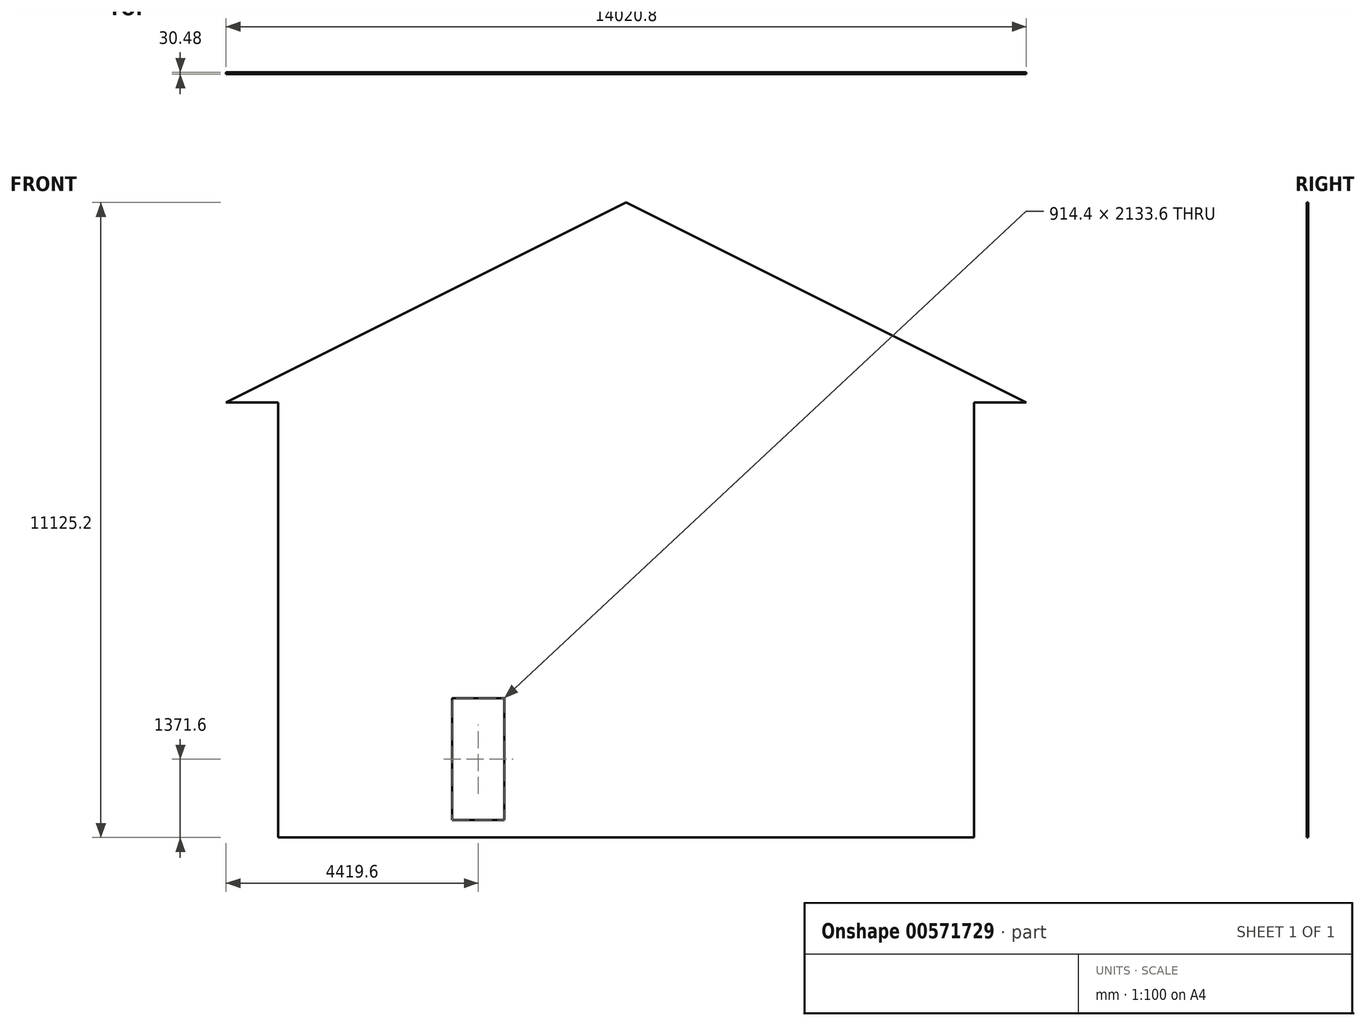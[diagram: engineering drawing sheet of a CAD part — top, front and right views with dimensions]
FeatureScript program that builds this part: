
annotation { "Feature Type Name" : "Feature", "Feature Type Description" : "" }
export const myFeature = defineFeature(function(context is Context, id is Id, definition is map)
    precondition{}
    {
        {
            var Q0;
            Q0=qCreatedBy(makeId("Front.planeOp"),FACE);
            var sketch = newSketch(context, id + "F0", { "sketchPlane" : qUnion([Q0])});
            skLineSegment(sketch, "E0", {"start": v(0, 0) * mm, "end": v(-12192, 0) * mm});
            skLineSegment(sketch, "E1", {"start": v(-12192, 0) * mm, "end": v(-12192, 304.8) * mm});
            skLineSegment(sketch, "E2", {"start": v(0, 0) * mm, "end": v(0, 304.8) * mm});
            skLineSegment(sketch, "E3", {"start": v(0, 304.8) * mm, "end": v(-12192, 304.8) * mm});
            skLineSegment(sketch, "E4", {"start": v(0, 304.8) * mm, "end": v(0, 7620) * mm});
            skLineSegment(sketch, "E5", {"start": v(-12192, 304.8) * mm, "end": v(-12192, 7620) * mm});
            skLineSegment(sketch, "E6", {"start": v(-12192, 7620) * mm, "end": v(0, 7620) * mm});
            skLineSegment(sketch, "E7", {"start": v(-12192, 7620) * mm, "end": v(-13106.4, 7620) * mm});
            skLineSegment(sketch, "E8", {"start": v(0, 7620) * mm, "end": v(914.4, 7620) * mm});
            skLineSegment(sketch, "E9", {"start": v(-6096, 7620) * mm, "end": v(-6096, 10668) * mm});
            skLineSegment(sketch, "E10", {"start": v(-6096, 10668) * mm, "end": v(-6096, 11125.2) * mm});
            skLineSegment(sketch, "E11", {"start": v(-12192, 7620) * mm, "end": v(-6096, 10668) * mm});
            skLineSegment(sketch, "E12", {"start": v(0, 7620) * mm, "end": v(-6096, 10668) * mm});
            skLineSegment(sketch, "E13", {"start": v(914.4, 7620) * mm, "end": v(-6096, 11125.2) * mm});
            skLineSegment(sketch, "E14", {"start": v(-13106.4, 7620) * mm, "end": v(-6096, 11125.2) * mm});
            skLineSegment(sketch, "E15", {"start": v(-9144, 304.8) * mm, "end": v(-9144, 2438.4) * mm});
            skLineSegment(sketch, "E16", {"start": v(-9144, 2438.4) * mm, "end": v(-8229.6, 2438.4) * mm});
            skLineSegment(sketch, "E17", {"start": v(-8229.6, 2438.4) * mm, "end": v(-8229.6, 304.8) * mm});
            skSolve(sketch);
        }
        {
            var Q0;
            Q0=makeQuery(id+"F0.imprint","IMPRINT",FACE,{"disambiguationData":[TD([[makeQuery(id+"F0.imprint","IMPRINT",EDGE,{"derivedFrom":sQuery(id+"F0.wireOp",EDGE,"E0")}),-1.0]])]});
            var Q1;
            Q1=makeQuery(id+"F0.imprint","IMPRINT",FACE,{"disambiguationData":[TD([[makeQuery(id+"F0.imprint","IMPRINT",EDGE,{"derivedFrom":sQuery(id+"F0.wireOp",EDGE,"E7")}),-1.0]])]});
            var Q2;
            Q2=makeQuery(id+"F0.imprint","IMPRINT",FACE,{"disambiguationData":[TD([[makeQuery(id+"F0.imprint","IMPRINT",EDGE,{"derivedFrom":sQuery(id+"F0.wireOp",EDGE,"E8")}),1.0]])]});
            var Q3;
            {var subQ2=sQuery(id+"F0.wireOp",EDGE,"E9");Q3=makeQuery(id+"F0.imprint","IMPRINT",FACE,{"disambiguationData":[TD([[makeQuery(id+"F0.imprint","IMPRINT",EDGE,{"derivedFrom":subQ2}),1.0]])]});}
            var Q4;
            {var subQ2=sQuery(id+"F0.wireOp",EDGE,"E9");Q4=makeQuery(id+"F0.imprint","IMPRINT",FACE,{"disambiguationData":[TD([[makeQuery(id+"F0.imprint","IMPRINT",EDGE,{"derivedFrom":subQ2}),-1.0]])]});}
            var Q5;
            {var subQ2=sQuery(id+"F0.wireOp",EDGE,"E4");Q5=makeQuery(id+"F0.imprint","IMPRINT",FACE,{"disambiguationData":[TD([[makeQuery(id+"F0.imprint","IMPRINT",EDGE,{"derivedFrom":subQ2}),1.0]])]});}
            extrude(context, id + "F1", {"entities" : qUnion([Q0, Q1, Q2, Q3, Q4, Q5]), "depth" : 30.48 * mm, "offsetDistance" : 30.48 * mm});
        }
    });
